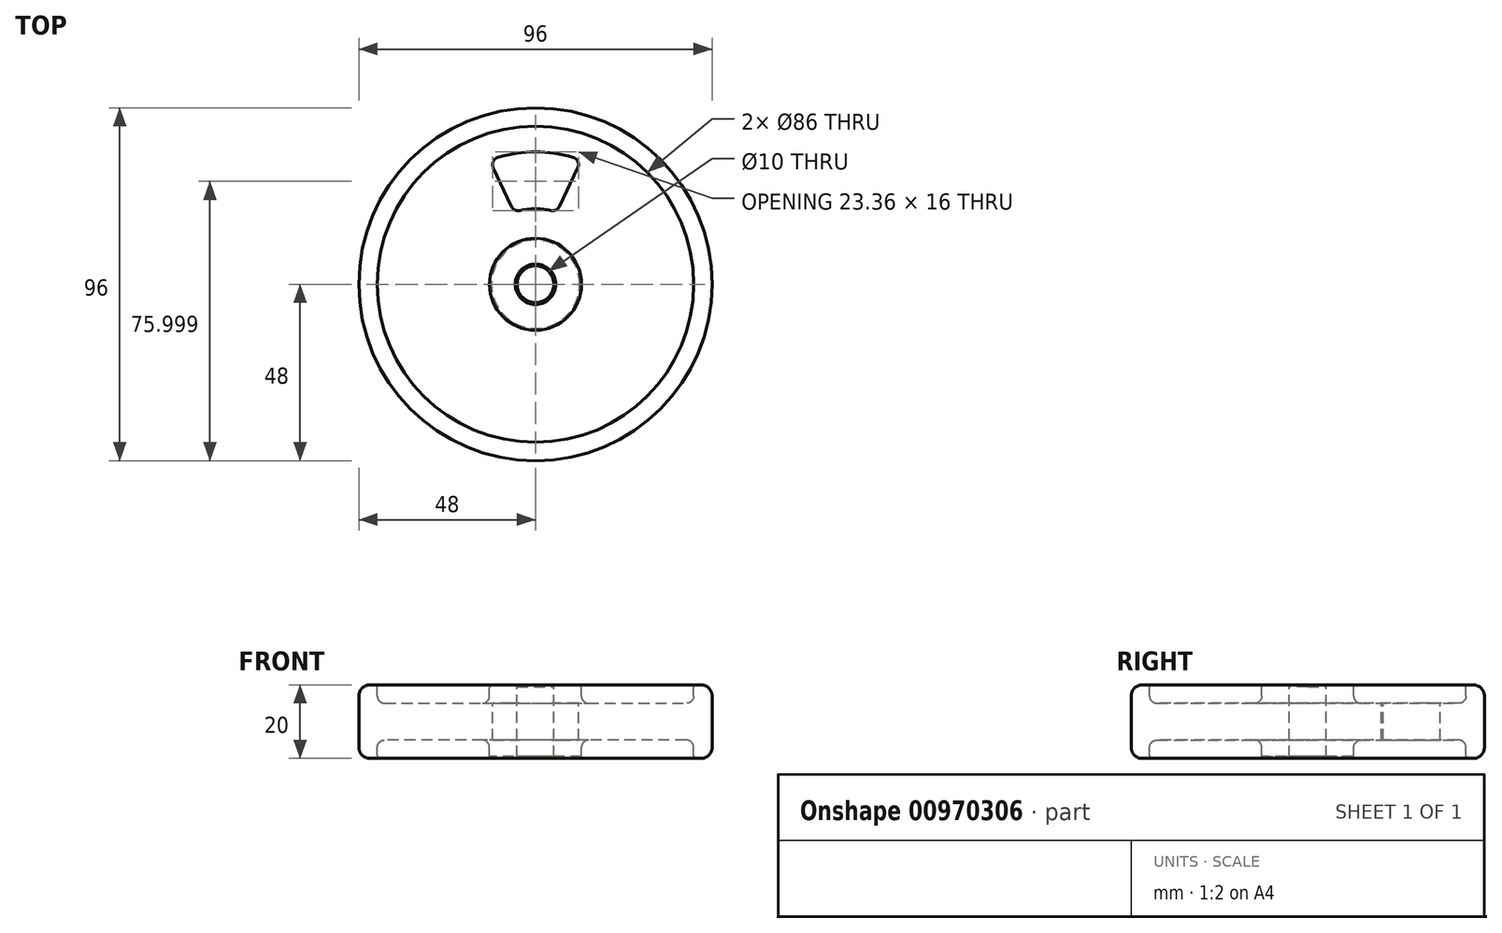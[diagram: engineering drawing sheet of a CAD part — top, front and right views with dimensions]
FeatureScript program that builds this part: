
annotation { "Feature Type Name" : "Feature", "Feature Type Description" : "" }
export const myFeature = defineFeature(function(context is Context, id is Id, definition is map)
    precondition{}
    {
        {
            var Q0;
            Q0=qCreatedBy(makeId("Front.planeOp"),FACE);
            var sketch = newSketch(context, id + "F0", { "sketchPlane" : qUnion([Q0])});
            skLineSegment(sketch, "E0", {"start": v(-5, 0) * mm, "end": v(-5, -20) * mm});
            skLineSegment(sketch, "E1", {"start": v(-5, -20) * mm, "end": v(-12.5, -20) * mm});
            skLineSegment(sketch, "E2", {"start": v(-12.5, -20) * mm, "end": v(-12.5, -15) * mm});
            skLineSegment(sketch, "E3", {"start": v(-12.5, -15) * mm, "end": v(-43, -15) * mm});
            skLineSegment(sketch, "E4", {"start": v(-43, -15) * mm, "end": v(-43, -20) * mm});
            skLineSegment(sketch, "E5", {"start": v(-43, -20) * mm, "end": v(-48, -20) * mm});
            skLineSegment(sketch, "E6", {"start": v(-48, -20) * mm, "end": v(-48, 0) * mm});
            skLineSegment(sketch, "E7", {"start": v(-48, 0) * mm, "end": v(-43, 0) * mm});
            skLineSegment(sketch, "E8", {"start": v(-43, 0) * mm, "end": v(-43, -5) * mm});
            skLineSegment(sketch, "E9", {"start": v(-43, -5) * mm, "end": v(-12.5, -5) * mm});
            skLineSegment(sketch, "E10", {"start": v(-12.5, -5) * mm, "end": v(-12.5, 0) * mm});
            skLineSegment(sketch, "E11", {"start": v(-12.5, 0) * mm, "end": v(-5, 0) * mm});
            skPoint(sketch, "E12.end.orphan", {"position": v(-12.5, -2.5) * mm});
            skLineSegment(sketch, "E13", {"start": v(0, 0) * mm, "end": v(0, -17.94) * mm});
            skSolve(sketch);
        }
        {
            var Q0;
            Q0=makeQuery(id+"F0.imprint","IMPRINT",FACE,{"disambiguationData":[TD([[makeQuery(id+"F0.imprint","IMPRINT",EDGE,{"derivedFrom":sQuery(id+"F0.wireOp",EDGE,"E0")}),-1.0]])]});
            var Q1;
            Q1=sQuery(id+"F0.wireOp",EDGE,"E13");
            revolve(context, id + "F1", {"surfaceOperationType" : NewSurfaceOperationType.NEW, "entities" : qUnion([Q0]), "axis" : qUnion([Q1]), "revolveType" : RevolveType.FULL});
        }
        {
            var Q0;
            Q0=makeQuery(id+"F1.opRevolve","SWEPT_EDGE",EDGE,{"disambiguationData":[OSD([sQuery(id+"F0.wireOp",EDGE,"E9"),sQuery(id+"F0.wireOp",EDGE,"E10")])]});
            var Q1;
            Q1=makeQuery(id+"F1.opRevolve","SWEPT_EDGE",EDGE,{"disambiguationData":[OSD([sQuery(id+"F0.wireOp",EDGE,"E8"),sQuery(id+"F0.wireOp",EDGE,"E9")])]});
            var Q2;
            Q2=makeQuery(id+"F1.opRevolve","SWEPT_EDGE",EDGE,{"disambiguationData":[OSD([sQuery(id+"F0.wireOp",EDGE,"E2"),sQuery(id+"F0.wireOp",EDGE,"E3")])]});
            var Q3;
            Q3=makeQuery(id+"F1.opRevolve","SWEPT_EDGE",EDGE,{"disambiguationData":[OSD([sQuery(id+"F0.wireOp",EDGE,"E3"),sQuery(id+"F0.wireOp",EDGE,"E4")])]});
            fillet(context, id + "F2", {"entities" : qUnion([Q0, Q1, Q2, Q3]), "radius" : 2 * mm, "tangentPropagation" : true, "allowEdgeOverflow" : false});
        }
        {
            var Q0;
            Q0=makeQuery(id+"F1.opRevolve","SWEPT_EDGE",EDGE,{"disambiguationData":[OSD([sQuery(id+"F0.wireOp",EDGE,"E6"),sQuery(id+"F0.wireOp",EDGE,"E7")])]});
            var Q1;
            Q1=makeQuery(id+"F1.opRevolve","SWEPT_EDGE",EDGE,{"disambiguationData":[OSD([sQuery(id+"F0.wireOp",EDGE,"E5"),sQuery(id+"F0.wireOp",EDGE,"E6")])]});
            fillet(context, id + "F3", {"entities" : qUnion([Q0, Q1]), "radius" : 3 * mm, "tangentPropagation" : true, "allowEdgeOverflow" : false});
        }
        {
            var Q0;
            Q0=makeQuery(id+"F1.opRevolve","SWEPT_FACE",FACE,{"disambiguationData":[OSD([sQuery(id+"F0.wireOp",EDGE,"E1")])]});
            var Q1;
            Q1=makeQuery(id+"F1.opRevolve","SWEPT_FACE",FACE,{"disambiguationData":[OSD([sQuery(id+"F0.wireOp",EDGE,"E0")])]});
            chamfer(context, id + "F4", {"entities" : qUnion([Q0, Q1]), "width" : .5 * mm, "tangentPropagation" : true});
        }
        {
            var Q0;
            Q0=makeQuery(id+"F1.opRevolve","SWEPT_FACE",FACE,{"disambiguationData":[OSD([sQuery(id+"F0.wireOp",EDGE,"E4")])]});
            var Q1;
            Q1=makeQuery(id+"F1.opRevolve","SWEPT_FACE",FACE,{"disambiguationData":[OSD([sQuery(id+"F0.wireOp",EDGE,"E8")])]});
            var Q2;
            Q2=makeQuery(id+"F1.opRevolve","SWEPT_EDGE",EDGE,{"disambiguationData":[OSD([sQuery(id+"F0.wireOp",EDGE,"E1"),sQuery(id+"F0.wireOp",EDGE,"E2")])]});
            var Q3;
            Q3=makeQuery(id+"F1.opRevolve","SWEPT_EDGE",EDGE,{"disambiguationData":[OSD([sQuery(id+"F0.wireOp",EDGE,"E10"),sQuery(id+"F0.wireOp",EDGE,"E11")])]});
            fillet(context, id + "F5", {"entities" : qUnion([Q0, Q1, Q2, Q3]), "radius" : .75 * mm, "tangentPropagation" : true, "allowEdgeOverflow" : false});
        }
        {
            var Q0;
            Q0=qCreatedBy(makeId("Top.planeOp"),FACE);
            var sketch = newSketch(context, id + "F6", { "sketchPlane" : qUnion([Q0])});
            skPoint(sketch, "E14.center", {"position": v(0, 0) * mm});
            skArc(sketch, "E15.0", {"start": v(10.25, 34.5) * mm, "mid": v(0, 36) * mm, "end": v(-10.25, 34.5) * mm});
            skArc(sketch, "E16.0", {"start": v(-10.25, 34.5) * mm, "mid": v(-11.5, 33.41) * mm, "end": v(-11.5, 31.75) * mm});
            skLineSegment(sketch, "E17.0", {"start": v(-11.5, 31.75) * mm, "end": v(-6.55, 21.15) * mm});
            skArc(sketch, "E18.0", {"start": v(-6.55, 21.15) * mm, "mid": v(-5.63, 20.2) * mm, "end": v(-4.32, 20.04) * mm});
            skArc(sketch, "E19.0", {"start": v(4.32, 20.04) * mm, "mid": v(0, 20.5) * mm, "end": v(-4.32, 20.04) * mm});
            skArc(sketch, "E20.0", {"start": v(4.32, 20.04) * mm, "mid": v(5.63, 20.2) * mm, "end": v(6.55, 21.15) * mm});
            skLineSegment(sketch, "E21.0", {"start": v(6.55, 21.15) * mm, "end": v(11.5, 31.75) * mm});
            skArc(sketch, "E22.0", {"start": v(11.5, 31.75) * mm, "mid": v(11.5, 33.41) * mm, "end": v(10.25, 34.5) * mm});
            skSolve(sketch);
        }
        {
            var Q0;
            Q0=qCreatedBy(makeId("Right.planeOp"),FACE);
            var sketch = newSketch(context, id + "F7", { "sketchPlane" : qUnion([Q0])});
            skLineSegment(sketch, "E23", {"start": v(0, 0) * mm, "end": v(0, -31.6) * mm});
            skSolve(sketch);
        }
        {
            var Q0;
            Q0=makeQuery(id+"F6.imprint","IMPRINT",FACE,{"disambiguationData":[TD([[makeQuery(id+"F6.imprint","IMPRINT",EDGE,{"derivedFrom":sQuery(id+"F6.wireOp",EDGE,"E15.0")}),1.0]])]});
            var Q1;
            Q1=makeQuery(id+"F3xeonLiqdhliLR_1.4.F6.imprint","IMPRINT",FACE,{"disambiguationData":[TD([[makeQuery(id+"F3xeonLiqdhliLR_1.4.F6.imprint","IMPRINT",EDGE,{"derivedFrom":sQuery(id+"F3xeonLiqdhliLR_1.4.F6.wireOp",EDGE,"E15.0")}),1.0]])]});
            var Q2;
            Q2=makeQuery(id+"F3xeonLiqdhliLR_1.3.F6.imprint","IMPRINT",FACE,{"disambiguationData":[TD([[makeQuery(id+"F3xeonLiqdhliLR_1.3.F6.imprint","IMPRINT",EDGE,{"derivedFrom":sQuery(id+"F3xeonLiqdhliLR_1.3.F6.wireOp",EDGE,"E15.0")}),1.0]])]});
            var Q3;
            Q3=makeQuery(id+"F3xeonLiqdhliLR_1.2.F6.imprint","IMPRINT",FACE,{"disambiguationData":[TD([[makeQuery(id+"F3xeonLiqdhliLR_1.2.F6.imprint","IMPRINT",EDGE,{"derivedFrom":sQuery(id+"F3xeonLiqdhliLR_1.2.F6.wireOp",EDGE,"E15.0")}),1.0]])]});
            var Q4;
            Q4=makeQuery(id+"F3xeonLiqdhliLR_1.1.F6.imprint","IMPRINT",FACE,{"disambiguationData":[TD([[makeQuery(id+"F3xeonLiqdhliLR_1.1.F6.imprint","IMPRINT",EDGE,{"derivedFrom":sQuery(id+"F3xeonLiqdhliLR_1.1.F6.wireOp",EDGE,"E15.0")}),1.0]])]});
            extrude(context, id + "F8", {"entities" : qUnion([Q0, Q1, Q2, Q3, Q4]), "operationType" : NewBodyOperationType.REMOVE, "endBound" : BoundingType.THROUGH_ALL, "oppositeDirection" : true, "depth" : 25 * mm, "offsetDistance" : 25 * mm});
        }
    });
